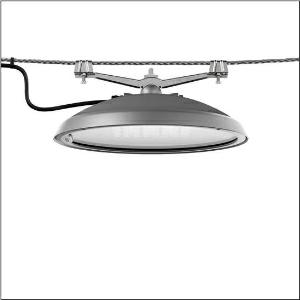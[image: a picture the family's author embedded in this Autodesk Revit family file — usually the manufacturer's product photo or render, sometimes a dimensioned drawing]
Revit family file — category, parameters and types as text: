
# Revit family: dl_r__50_iq_mini___st1_0s_5xa248w41f08re_89db
name_source: partatom
category: Lighting Fixtures
units: mm (PartAtom-declared; Revit-internal decimal feet)

## family parameters
Cut with Voids When Loaded = No
Host = Face
Light Source = No
Part Type = Normal
Room Calculation Point = No
Round Connector Dimension = Use Diameter
Shared = No

## types (1)
- --- (1 x LED, 5990 lm, 33.8 W, 4000K)
    Apparent Load = 34 VA
    CIE Flux Codes = 37 72 97 100 100
    Color Rendering = 70
    Color Temperature = 4000K
    Default Elevation = 1800 mm
    Description = DL® 50 iQ mini, catenary luminaire, primary light control with lens, of PMMA, primary optical cover: cover, of toughened safety glass, transparent, light distribution: ST1.0s, light emission: direct distribution, primary light characteristic: symmetric, installation type: suspended mounting, LED, High Power LED, rated luminous flux: 5.990lm, luminous efficacy: 177lm/W, light colour: 740, colour temperature: 4000K, control: optimised constant luminous flux control (CLO 2.0), Desk-Remote (wireless, voltage-free reading and setting of iQ features in the workshop via application-optimized NFC function/RFID function), Light-Fading, Smart-Wire, Night-Set, Lumen-Switch, Temp-Guard, Auto-Match, Street-Remote, mains connection: 230..240V, AC, 50/60Hz, start of lifetime: 34W, end of service life: 35W, reduction: 16W, luminaire housing, of diecast aluminium, powder-coated, Siteco® metallic grey (DB 702S), diameter: 500mm, height: 115mm, protection rating (complete): IP66, insulation class (complete): insulation class II (safety insulation), certification: CE, ENEC, VDE, impact resistance: IK08, permissible operating ambient temperature for outdoor applications: -25..+40°C, standard-compliant lighting for roads and squares, packaging unit: 1 piece

Light Distribution: ST1.0s
    Height = 124 mm  [stored 0.406824 ft]
    Lamp = 1 x LED
    Lamp Light Flux = 5990 lm
    Lamp Power = 33.8 W
    Lamp count = 1
    Length = 500 mm
    Luminous efficacy = 177 lm/W
    Manufacturer = Siteco
    ModVariant = No
    Model = 5XA248W41F08RE
    Number of Poles = 1
    OnlyDefault = Yes
    Power Factor = 1
    Product Name = DL® 50 iQ mini | ST1.0s
    Product group = catenary luminaire
    ProductGroupID = 6300
    Protection Class = Protection class II
    Protection Degree = IP 66
    RLX_Detail_Level = 1
    RLX_Emergency_Light_Flux = 0 lm
    RLX_Emergency_Type = 0
    RLX_Emergency_Type_DB = No
    RlxData = <blob elided: 123561 chars, md5=60bf65e6>
    Socket = socket
    Standby Power = 0 W
    System Light Flux = 5990 lm
    System Power = 34 W
    Type Comments = factory setting: luminous flux: 100 % | dim-lin: 254 | 359 mA
    Type Image = l_1242791.jpg
    URL = http://relux.com
    VarID = @adj_090085
    Voltage = 0 V
    Weight = 0.00 kg
    Width = 0 mm  [stored 0 ft]

note: [stored X ft] marks values corroborated as IEEE doubles in the binary element streams (Revit-internal decimal feet)

## geometry (parser evidence)
native form markers: Blend x4, Sweep x11
no freeform markers — native parametric forms only
